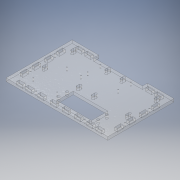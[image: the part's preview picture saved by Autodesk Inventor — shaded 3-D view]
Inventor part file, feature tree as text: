
AUTODESK INVENTOR PART (.ipt)
format: ipt  version: 2019 (Build 230136000, 136)  size: 337,920 bytes
history: native  units: mm
features: extrude x1, sketch x1
ambient origin geometry x8: Origin, YZ Plane, XZ Plane, XY Plane, X Axis, Y Axis, Z Axis, Center Point
bodies: Body1 (feature_tree)
feature tree (2):
  extrude  "Extrusion3"  Depth=200.0mm
  sketch  "Sketch1"  dims[d0=130.0mm d1=200.0mm d7=1.8mm d8=5.1mm d9=27.9mm d10=1.3mm d11=50.8mm d12=15.2mm d14=26.0mm d23=4.8mm d31=5.1mm d32=4.45mm d34=6.15mm d35=11.7mm d36=12.3mm d37=11.7mm d43=11.7mm d44=6.3mm d45=11.7mm d48=6.0mm d49=0.0mm d50=2.5mm d54=10.5mm d55=32.0mm d56=68.0mm d58=5.0mm d62=17.0mm d63=5.0mm d64=12.3mm d65=11.7mm d66=5.1mm d67=12.3mm d68=11.7mm d69=12.3mm d70=11.7mm d71=12.3mm d72=11.7mm d73=4.45mm d74=6.3mm d75=6.3mm d77=15.0mm d78=67.0mm d79=5.0mm d80=25.0mm d81=60.0mm d82=2.25mm d83=6.15mm d84=2.55mm d85=2.25mm d86=2.25mm d87=2.55mm d88=6.15mm d89=7.0mm d90=56.0mm d91=15.0mm d92=2.0mm d93=22.5mm]
